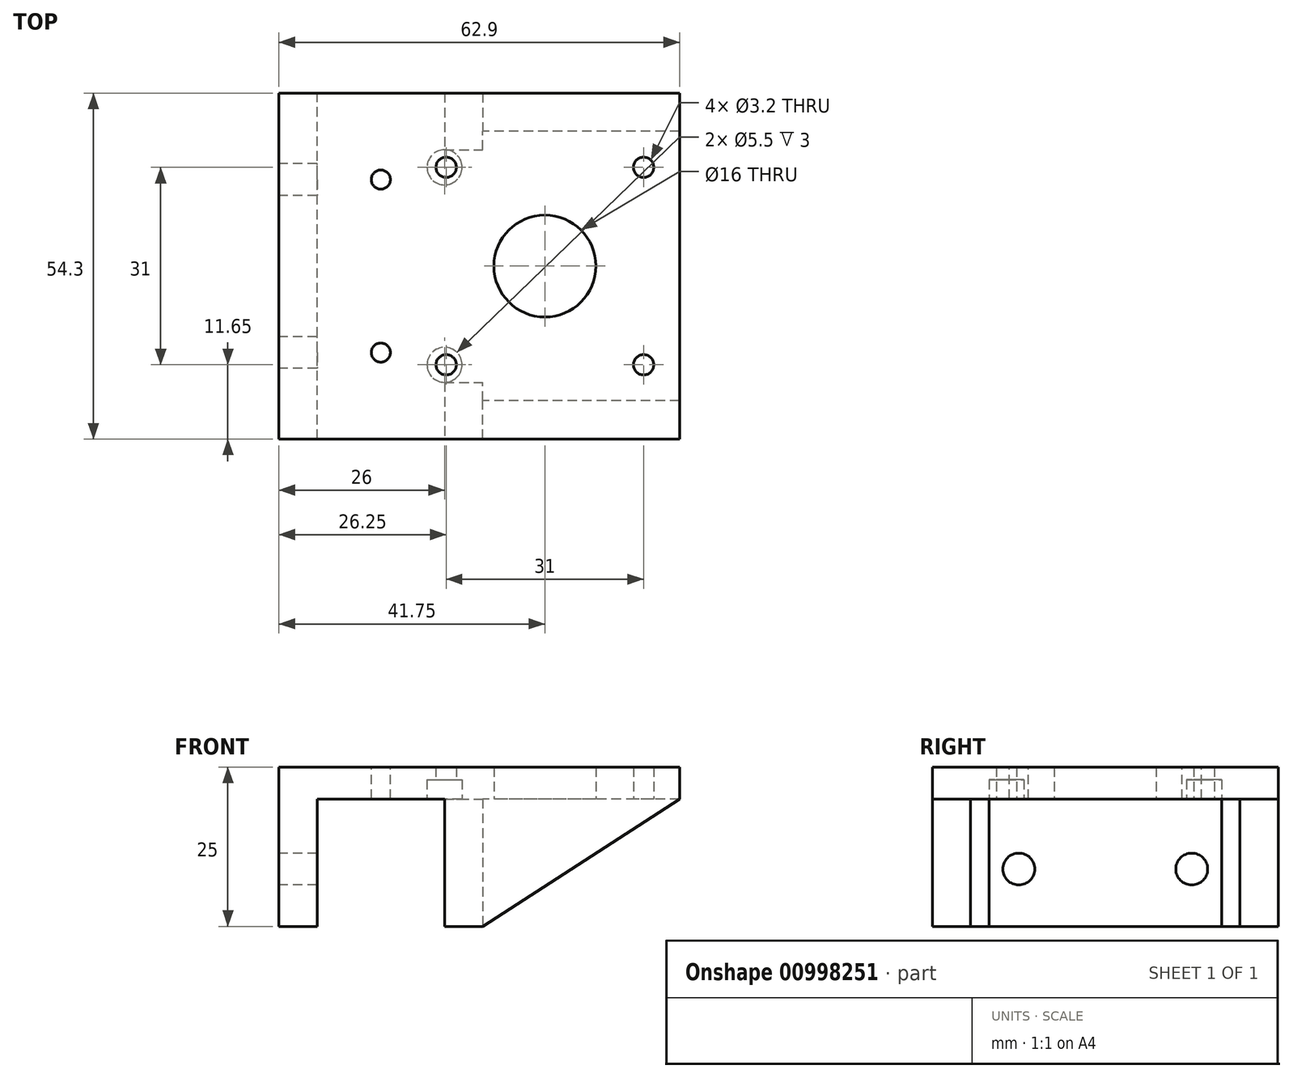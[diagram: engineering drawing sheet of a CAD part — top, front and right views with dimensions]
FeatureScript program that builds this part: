
annotation { "Feature Type Name" : "Feature", "Feature Type Description" : "" }
export const myFeature = defineFeature(function(context is Context, id is Id, definition is map)
    precondition{}
    {
        {
            var Q0;
            Q0=qCreatedBy(makeId("Top.planeOp"),FACE);
            var sketch = newSketch(context, id + "F0", { "sketchPlane" : qUnion([Q0])});
            skPoint(sketch, "E0.middle", {"position": v(0, 0) * mm});
            skCircle(sketch, "E1", {"center": v(0, 0) * mm, "radius": 8 * mm});
            skLineSegment(sketch, "E2.bottom", {"start": v(21.15, -21.15) * mm, "end": v(-21.15, -21.15) * mm});
            skLineSegment(sketch, "E2.top", {"start": v(21.15, 21.15) * mm, "end": v(-21.15, 21.15) * mm});
            skLineSegment(sketch, "E2.left", {"start": v(21.15, -21.15) * mm, "end": v(21.15, 21.15) * mm});
            skLineSegment(sketch, "E3.bottom", {"start": v(-9.75, -21.15) * mm, "end": v(-41.75, -21.15) * mm});
            skLineSegment(sketch, "E3.top", {"start": v(-9.75, 21.15) * mm, "end": v(-41.75, 21.15) * mm});
            skLineSegment(sketch, "E3.left", {"start": v(-9.75, -21.15) * mm, "end": v(-9.75, 21.15) * mm});
            skLineSegment(sketch, "E3.right", {"start": v(-41.75, -21.15) * mm, "end": v(-41.75, 21.15) * mm});
            skCircle(sketch, "E4", {"center": v(-15.5, 15.5) * mm, "radius": 1.6 * mm});
            skCircle(sketch, "E5", {"center": v(15.5, 15.5) * mm, "radius": 1.6 * mm});
            skCircle(sketch, "E6", {"center": v(15.5, -15.5) * mm, "radius": 1.6 * mm});
            skCircle(sketch, "E7", {"center": v(-15.5, -15.5) * mm, "radius": 1.6 * mm});
            skSolve(sketch);
        }
        {
            var Q0;
            Q0=makeQuery(id+"F0.imprint","IMPRINT",FACE,{"disambiguationData":[TD([[makeQuery(id+"F0.imprint","IMPRINT",EDGE,{"derivedFrom":sQuery(id+"F0.wireOp",EDGE,"E1")}),-1.0]])]});
            var Q1;
            {var subQ1=sQuery(id+"F0.wireOp",EDGE,"E3.left");Q1=makeQuery(id+"F0.imprint","IMPRINT",FACE,{"disambiguationData":[TD([[makeQuery(id+"F0.imprint","IMPRINT",EDGE,{"derivedFrom":subQ1}),1.0]])]});}
            extrude(context, id + "F1", {"entities" : qUnion([Q0, Q1]), "depth" : 5 * mm, "offsetDistance" : 25 * mm});
        }
        {
            var Q0;
            Q0=makeQuery(id+"F1.opExtrude","CAP_FACE",FACE,{"disambiguationData":[OSD([sQuery(id+"F0.wireOp",EDGE,"E1"),sQuery(id+"F0.wireOp",EDGE,"E2.bottom"),sQuery(id+"F0.wireOp",EDGE,"E2.top"),sQuery(id+"F0.wireOp",EDGE,"E2.left"),sQuery(id+"F0.wireOp",EDGE,"E3.bottom"),sQuery(id+"F0.wireOp",EDGE,"E3.top"),sQuery(id+"F0.wireOp",EDGE,"E3.right"),sQuery(id+"F0.wireOp",EDGE,"E4"),sQuery(id+"F0.wireOp",EDGE,"E5"),sQuery(id+"F0.wireOp",EDGE,"E6"),sQuery(id+"F0.wireOp",EDGE,"E7")])],"isStart":true});
            var sketch = newSketch(context, id + "F2", { "sketchPlane" : qUnion([Q0])});
            skLineSegment(sketch, "E8", {"start": v(-41.75, 21.15) * mm, "end": v(-35.75, 21.15) * mm});
            skLineSegment(sketch, "E9", {"start": v(-35.75, 21.15) * mm, "end": v(-35.75, -21.15) * mm});
            skLineSegment(sketch, "E10", {"start": v(-35.75, -21.15) * mm, "end": v(-15.75, -21.15) * mm});
            skLineSegment(sketch, "E11", {"start": v(-15.75, -21.15) * mm, "end": v(-15.75, 21.15) * mm});
            skLineSegment(sketch, "E12", {"start": v(-15.75, 21.15) * mm, "end": v(-9.75, 21.15) * mm});
            skLineSegment(sketch, "E13", {"start": v(-9.75, 21.15) * mm, "end": v(-9.75, -21.15) * mm});
            skSolve(sketch);
        }
        {
            var Q0;
            Q0=makeQuery(id+"F2.imprint","IMPRINT",FACE,{"disambiguationData":[TD([[makeQuery(id+"F2.imprint","IMPRINT",EDGE,{"derivedFrom":sQuery(id+"F2.wireOp",EDGE,"E8")}),1.0]])]});
            var Q1;
            {var subQ0=sQuery(id+"F2.wireOp",EDGE,"E12");Q1=makeQuery(id+"F2.imprint","IMPRINT",FACE,{"disambiguationData":[TD([[makeQuery(id+"F2.imprint","IMPRINT",EDGE,{"derivedFrom":subQ0}),1.0]])]});}
            extrude(context, id + "F3", {"entities" : qUnion([Q0, Q1]), "operationType" : NewBodyOperationType.ADD, "depth" : 20 * mm, "offsetDistance" : 25 * mm});
        }
        {
            var Q0;
            {var subQ1=sQuery(id+"F0.wireOp",EDGE,"E3.top");var subQ2=sQuery(id+"F0.wireOp",EDGE,"E2.top");var subQ3=makeQuery(id+"F1.opExtrude","CAP_EDGE",EDGE,{"disambiguationData":[OSD([subQ2,subQ1])],"isStart":true});Q0=makeQuery(id+"F3.boolean.opBoolean","MERGE",FACE,{"derivedFrom":[makeQuery(id+"F1.opExtrude","SWEPT_FACE",FACE,{"disambiguationData":[OSD([subQ2,subQ1])]}),makeQuery(id+"F3.opExtrude","SWEPT_FACE",FACE,{"disambiguationData":[OSD([subQ2,subQ1]),TDD([makeQuery(id+"F2.imprint","IMPRINT",EDGE,{"disambiguationData":[TD([[makeQuery(id+"F2.imprint","INTERSECT",VERTEX,{"derivedFrom":[subQ3,makeQuery(id+"F1.opExtrude","CAP_EDGE",EDGE,{"disambiguationData":[OSD([sQuery(id+"F0.wireOp",EDGE,"E3.right")])],"isStart":true})]}),1.0]])],"derivedFrom":subQ3})])]}),makeQuery(id+"F3.opExtrude","SWEPT_FACE",FACE,{"disambiguationData":[OSD([subQ2,subQ1]),TDD([makeQuery(id+"F2.imprint","IMPRINT",EDGE,{"disambiguationData":[TD([[makeQuery(id+"F2.imprint","INTERSECT",VERTEX,{"derivedFrom":[subQ3,sQuery(id+"F2.wireOp",EDGE,"E13")]}),-1.0]])],"derivedFrom":subQ3})])]})]});}
            var sketch = newSketch(context, id + "F4", { "sketchPlane" : qUnion([Q0])});
            skLineSegment(sketch, "E14", {"start": v(9.75, -20) * mm, "end": v(-21.15, 0) * mm});
            skSolve(sketch);
        }
        {
            var Q0;
            Q0=makeQuery(id+"F4.imprint","IMPRINT",FACE,{"disambiguationData":[TD([[makeQuery(id+"F4.imprint","IMPRINT",EDGE,{"derivedFrom":sQuery(id+"F4.wireOp",EDGE,"E14")}),-1.0]])]});
            var Q1;
            {var subQ3=sQuery(id+"F0.wireOp",EDGE,"E2.top");var subQ5=sQuery(id+"F0.wireOp",EDGE,"E2.left");Q1=makeQuery(id+"F4.imprint","IMPRINT",FACE,{"disambiguationData":[TD([[makeQuery(id+"F4.imprint","IMPRINT",EDGE,{"derivedFrom":makeQuery(id+"F1.opExtrude","SWEPT_EDGE",EDGE,{"disambiguationData":[OSD([subQ3,subQ5])]})}),1.0]])]});}
            extrude(context, id + "F5", {"entities" : qUnion([Q0, Q1]), "operationType" : NewBodyOperationType.ADD, "depth" : 6 * mm, "offsetDistance" : 25 * mm});
        }
        {
            var Q0;
            Q0=makeQuery(id+"F3.boolean.opBoolean","MERGE",FACE,{"derivedFrom":[makeQuery(id+"F1.opExtrude","SWEPT_FACE",FACE,{"disambiguationData":[OSD([sQuery(id+"F0.wireOp",EDGE,"E2.bottom"),sQuery(id+"F0.wireOp",EDGE,"E3.bottom")])]}),makeQuery(id+"F3.opExtrude","SWEPT_FACE",FACE,{"disambiguationData":[OSD([sQuery(id+"F2.wireOp",EDGE,"E8")])]}),makeQuery(id+"F3.opExtrude","SWEPT_FACE",FACE,{"disambiguationData":[OSD([sQuery(id+"F2.wireOp",EDGE,"E12")])]})]});
            var sketch = newSketch(context, id + "F6", { "sketchPlane" : qUnion([Q0])});
            skLineSegment(sketch, "E15", {"start": v(-9.75, -20) * mm, "end": v(21.15, 0) * mm});
            skSolve(sketch);
        }
        {
            var Q0;
            Q0=makeQuery(id+"F6.imprint","IMPRINT",FACE,{"disambiguationData":[TD([[makeQuery(id+"F6.imprint","IMPRINT",EDGE,{"derivedFrom":sQuery(id+"F6.wireOp",EDGE,"E15")}),1.0]])]});
            var Q1;
            {var subQ5=sQuery(id+"F2.wireOp",EDGE,"E8");Q1=makeQuery(id+"F6.imprint","IMPRINT",FACE,{"disambiguationData":[TD([[makeQuery(id+"F6.imprint","IMPRINT",EDGE,{"derivedFrom":makeQuery(id+"F3.opExtrude","CAP_EDGE",EDGE,{"disambiguationData":[OSD([subQ5])],"isStart":false})}),-1.0]])]});}
            extrude(context, id + "F7", {"entities" : qUnion([Q0, Q1]), "operationType" : NewBodyOperationType.ADD, "depth" : 6 * mm, "offsetDistance" : 25 * mm});
        }
        {
            var Q0;
            {var subQ0=sQuery(id+"F0.wireOp",EDGE,"E3.right");Q0=makeQuery(id+"F7.boolean.opBoolean","MERGE",FACE,{"derivedFrom":[makeQuery(id+"F5.boolean.opBoolean","MERGE",FACE,{"derivedFrom":[makeQuery(id+"F3.boolean.opBoolean","MERGE",FACE,{"derivedFrom":[makeQuery(id+"F1.opExtrude","SWEPT_FACE",FACE,{"disambiguationData":[OSD([subQ0])]}),makeQuery(id+"F3.opExtrude","SWEPT_FACE",FACE,{"disambiguationData":[OSD([subQ0])]})]}),makeQuery(id+"F5.opExtrude","SWEPT_FACE",FACE,{"disambiguationData":[OSD([sQuery(id+"F0.wireOp",EDGE,"E2.top"),sQuery(id+"F0.wireOp",EDGE,"E3.top"),subQ0])]})]}),makeQuery(id+"F7.opExtrude","SWEPT_FACE",FACE,{"disambiguationData":[OSD([sQuery(id+"F0.wireOp",EDGE,"E3.bottom"),subQ0,sQuery(id+"F2.wireOp",EDGE,"E8")])]})]});}
            var sketch = newSketch(context, id + "F8", { "sketchPlane" : qUnion([Q0])});
            skLineSegment(sketch, "E16", {"start": v(27.15, 5) * mm, "end": v(27.15, -1) * mm});
            skLineSegment(sketch, "E17", {"start": v(27.15, -1) * mm, "end": v(27.15, -11) * mm});
            skCircle(sketch, "E18", {"center": v(13.58, -11) * mm, "radius": 2.5 * mm});
            skCircle(sketch, "E19", {"center": v(-13.57, -11) * mm, "radius": 2.5 * mm});
            skSolve(sketch);
        }
        {
            var Q0;
            Q0=makeQuery(id+"F8.imprint","IMPRINT",FACE,{"disambiguationData":[TD([[makeQuery(id+"F8.imprint","IMPRINT",EDGE,{"derivedFrom":sQuery(id+"F8.wireOp",EDGE,"E18")}),1.0]])]});
            var Q1;
            Q1=makeQuery(id+"F8.imprint","IMPRINT",FACE,{"disambiguationData":[TD([[makeQuery(id+"F8.imprint","IMPRINT",EDGE,{"derivedFrom":sQuery(id+"F8.wireOp",EDGE,"E19")}),1.0]])]});
            extrude(context, id + "F9", {"entities" : qUnion([Q0, Q1]), "operationType" : NewBodyOperationType.REMOVE, "oppositeDirection" : true, "depth" : 25 * mm, "offsetDistance" : 25 * mm});
        }
        {
            var Q0;
            {var subQ0=sQuery(id+"F2.wireOp",EDGE,"E12");var subQ1=sQuery(id+"F2.wireOp",EDGE,"E11");var subQ2=sQuery(id+"F0.wireOp",EDGE,"E3.top");var subQ3=sQuery(id+"F0.wireOp",EDGE,"E2.top");var subQ4=makeQuery(id+"F1.opExtrude","CAP_EDGE",EDGE,{"disambiguationData":[OSD([subQ3,subQ2])],"isStart":true});var subQ5=sQuery(id+"F2.wireOp",EDGE,"E13");Q0=makeQuery(id+"F7.boolean.opBoolean","MERGE",FACE,{"derivedFrom":[makeQuery(id+"F5.boolean.opBoolean","MERGE",FACE,{"derivedFrom":[makeQuery(id+"F3.opExtrude","CAP_FACE",FACE,{"disambiguationData":[OSD([subQ3,subQ2,sQuery(id+"F0.wireOp",EDGE,"E4"),sQuery(id+"F0.wireOp",EDGE,"E7"),subQ1,subQ0,subQ5])],"isStart":false}),makeQuery(id+"F5.opExtrude","SWEPT_FACE",FACE,{"disambiguationData":[OSD([subQ3,subQ2]),TDD([makeQuery(id+"F4.imprint","IMPRINT",EDGE,{"derivedFrom":makeQuery(id+"F3.opExtrude","CAP_EDGE",EDGE,{"disambiguationData":[OSD([subQ3,subQ2]),TDD([makeQuery(id+"F2.imprint","IMPRINT",EDGE,{"disambiguationData":[TD([[makeQuery(id+"F2.imprint","INTERSECT",VERTEX,{"derivedFrom":[subQ4,subQ5]}),-1.0]])],"derivedFrom":subQ4})])],"isStart":false})})])]})]}),makeQuery(id+"F7.opExtrude","SWEPT_FACE",FACE,{"disambiguationData":[OSD([subQ0])]})]});}
            var sketch = newSketch(context, id + "F10", { "sketchPlane" : qUnion([Q0])});
            skCircle(sketch, "E20", {"center": v(-15.75, -15.5) * mm, "radius": 2.75 * mm});
            skCircle(sketch, "E21", {"center": v(-15.75, 15.5) * mm, "radius": 2.75 * mm});
            skSolve(sketch);
        }
        {
            var Q0;
            {var subQ2=sQuery(id+"F0.wireOp",EDGE,"E4");var subQ13=makeQuery(id+"F3.opExtrude","CAP_EDGE",EDGE,{"disambiguationData":[OSD([subQ2])],"isStart":false});Q0=makeQuery(id+"F10.imprint","IMPRINT",FACE,{"disambiguationData":[TD([[makeQuery(id+"F10.imprint","IMPRINT",EDGE,{"derivedFrom":subQ13}),1.0]])]});}
            var Q1;
            {var subQ2=sQuery(id+"F0.wireOp",EDGE,"E4");var subQ13=makeQuery(id+"F3.opExtrude","CAP_EDGE",EDGE,{"disambiguationData":[OSD([subQ2])],"isStart":false});Q1=makeQuery(id+"F10.imprint","IMPRINT",FACE,{"disambiguationData":[TD([[makeQuery(id+"F10.imprint","IMPRINT",EDGE,{"derivedFrom":subQ13}),-1.0]])]});}
            extrude(context, id + "F11", {"entities" : qUnion([Q0, Q1]), "operationType" : NewBodyOperationType.REMOVE, "oppositeDirection" : true, "depth" : 23 * mm, "offsetDistance" : 25 * mm});
        }
        {
            var Q0;
            {var subQ0=sQuery(id+"F2.wireOp",EDGE,"E12");var subQ1=sQuery(id+"F2.wireOp",EDGE,"E11");var subQ2=sQuery(id+"F0.wireOp",EDGE,"E3.top");var subQ3=sQuery(id+"F0.wireOp",EDGE,"E2.top");var subQ4=makeQuery(id+"F1.opExtrude","CAP_EDGE",EDGE,{"disambiguationData":[OSD([subQ3,subQ2])],"isStart":true});var subQ5=sQuery(id+"F2.wireOp",EDGE,"E13");Q0=makeQuery(id+"F7.boolean.opBoolean","MERGE",FACE,{"derivedFrom":[makeQuery(id+"F5.boolean.opBoolean","MERGE",FACE,{"derivedFrom":[makeQuery(id+"F3.opExtrude","CAP_FACE",FACE,{"disambiguationData":[OSD([subQ3,subQ2,sQuery(id+"F0.wireOp",EDGE,"E4"),sQuery(id+"F0.wireOp",EDGE,"E7"),subQ1,subQ0,subQ5])],"isStart":false}),makeQuery(id+"F5.opExtrude","SWEPT_FACE",FACE,{"disambiguationData":[OSD([subQ3,subQ2]),TDD([makeQuery(id+"F4.imprint","IMPRINT",EDGE,{"derivedFrom":makeQuery(id+"F3.opExtrude","CAP_EDGE",EDGE,{"disambiguationData":[OSD([subQ3,subQ2]),TDD([makeQuery(id+"F2.imprint","IMPRINT",EDGE,{"disambiguationData":[TD([[makeQuery(id+"F2.imprint","INTERSECT",VERTEX,{"derivedFrom":[subQ4,subQ5]}),-1.0]])],"derivedFrom":subQ4})])],"isStart":false})})])]})]}),makeQuery(id+"F7.opExtrude","SWEPT_FACE",FACE,{"disambiguationData":[OSD([subQ0])]})]});}
            var sketch = newSketch(context, id + "F12", { "sketchPlane" : qUnion([Q0])});
            skCircle(sketch, "E22", {"center": v(-15.75, 15.5) * mm, "radius": 2.75 * mm});
            skSolve(sketch);
        }
        {
            var Q0;
            {var subQ5=sQuery(id+"F0.wireOp",EDGE,"E7");var subQ11=makeQuery(id+"F3.opExtrude","CAP_EDGE",EDGE,{"disambiguationData":[OSD([subQ5])],"isStart":false});Q0=makeQuery(id+"F12.imprint","IMPRINT",FACE,{"disambiguationData":[TD([[makeQuery(id+"F12.imprint","IMPRINT",EDGE,{"derivedFrom":subQ11}),1.0]])]});}
            var Q1;
            {var subQ5=sQuery(id+"F0.wireOp",EDGE,"E7");var subQ11=makeQuery(id+"F3.opExtrude","CAP_EDGE",EDGE,{"disambiguationData":[OSD([subQ5])],"isStart":false});Q1=makeQuery(id+"F12.imprint","IMPRINT",FACE,{"disambiguationData":[TD([[makeQuery(id+"F12.imprint","IMPRINT",EDGE,{"derivedFrom":subQ11}),-1.0]])]});}
            extrude(context, id + "F13", {"entities" : qUnion([Q0, Q1]), "operationType" : NewBodyOperationType.REMOVE, "oppositeDirection" : true, "depth" : 23 * mm, "offsetDistance" : 25 * mm});
        }
        {
            var Q0;
            {var subQ0=sQuery(id+"F2.wireOp",EDGE,"E12");var subQ1=sQuery(id+"F2.wireOp",EDGE,"E11");var subQ2=sQuery(id+"F0.wireOp",EDGE,"E3.top");var subQ3=sQuery(id+"F0.wireOp",EDGE,"E2.top");var subQ4=makeQuery(id+"F1.opExtrude","CAP_EDGE",EDGE,{"disambiguationData":[OSD([subQ3,subQ2])],"isStart":true});var subQ5=sQuery(id+"F2.wireOp",EDGE,"E13");Q0=makeQuery(id+"F7.boolean.opBoolean","MERGE",FACE,{"derivedFrom":[makeQuery(id+"F5.boolean.opBoolean","MERGE",FACE,{"derivedFrom":[makeQuery(id+"F3.opExtrude","CAP_FACE",FACE,{"disambiguationData":[OSD([subQ3,subQ2,sQuery(id+"F0.wireOp",EDGE,"E4"),sQuery(id+"F0.wireOp",EDGE,"E7"),subQ1,subQ0,subQ5])],"isStart":false}),makeQuery(id+"F5.opExtrude","SWEPT_FACE",FACE,{"disambiguationData":[OSD([subQ3,subQ2]),TDD([makeQuery(id+"F4.imprint","IMPRINT",EDGE,{"derivedFrom":makeQuery(id+"F3.opExtrude","CAP_EDGE",EDGE,{"disambiguationData":[OSD([subQ3,subQ2]),TDD([makeQuery(id+"F2.imprint","IMPRINT",EDGE,{"disambiguationData":[TD([[makeQuery(id+"F2.imprint","INTERSECT",VERTEX,{"derivedFrom":[subQ4,subQ5]}),-1.0]])],"derivedFrom":subQ4})])],"isStart":false})})])]})]}),makeQuery(id+"F7.opExtrude","SWEPT_FACE",FACE,{"disambiguationData":[OSD([subQ0])]})]});}
            var sketch = newSketch(context, id + "F14", { "sketchPlane" : qUnion([Q0])});
            skLineSegment(sketch, "E23", {"start": v(-15.75, 18.25) * mm, "end": v(-9.75, 18.25) * mm});
            skLineSegment(sketch, "E24", {"start": v(-15.75, -18.25) * mm, "end": v(-9.75, -18.25) * mm});
            skSolve(sketch);
        }
        {
            var Q0;
            {var subQ1=sQuery(id+"F14.wireOp",EDGE,"E23");Q0=makeQuery(id+"F14.imprint","IMPRINT",FACE,{"disambiguationData":[TD([[makeQuery(id+"F14.imprint","IMPRINT",EDGE,{"derivedFrom":subQ1}),-1.0]])]});}
            extrude(context, id + "F15", {"entities" : qUnion([Q0]), "operationType" : NewBodyOperationType.REMOVE, "oppositeDirection" : true, "depth" : 20 * mm, "offsetDistance" : 25 * mm});
        }
        {
            var Q0;
            {var subQ0=sQuery(id+"F0.wireOp",EDGE,"E3.bottom");var subQ1=sQuery(id+"F0.wireOp",EDGE,"E2.bottom");var subQ2=sQuery(id+"F0.wireOp",EDGE,"E3.top");var subQ3=sQuery(id+"F0.wireOp",EDGE,"E2.top");Q0=makeQuery(id+"F7.boolean.opBoolean","MERGE",FACE,{"derivedFrom":[makeQuery(id+"F5.boolean.opBoolean","MERGE",FACE,{"derivedFrom":[makeQuery(id+"F1.opExtrude","CAP_FACE",FACE,{"disambiguationData":[OSD([sQuery(id+"F0.wireOp",EDGE,"E1"),subQ1,subQ3,sQuery(id+"F0.wireOp",EDGE,"E2.left"),subQ0,subQ2,sQuery(id+"F0.wireOp",EDGE,"E3.right"),sQuery(id+"F0.wireOp",EDGE,"E4"),sQuery(id+"F0.wireOp",EDGE,"E5"),sQuery(id+"F0.wireOp",EDGE,"E6"),sQuery(id+"F0.wireOp",EDGE,"E7")])],"isStart":false}),makeQuery(id+"F5.opExtrude","SWEPT_FACE",FACE,{"disambiguationData":[OSD([subQ3,subQ2]),TDD([makeQuery(id+"F4.imprint","IMPRINT",EDGE,{"derivedFrom":makeQuery(id+"F1.opExtrude","CAP_EDGE",EDGE,{"disambiguationData":[OSD([subQ3,subQ2])],"isStart":false})})])]})]}),makeQuery(id+"F7.opExtrude","SWEPT_FACE",FACE,{"disambiguationData":[OSD([subQ1,subQ0]),TDD([makeQuery(id+"F6.imprint","IMPRINT",EDGE,{"derivedFrom":makeQuery(id+"F1.opExtrude","CAP_EDGE",EDGE,{"disambiguationData":[OSD([subQ1,subQ0])],"isStart":false})})])]})]});}
            var sketch = newSketch(context, id + "F16", { "sketchPlane" : qUnion([Q0])});
            skLineSegment(sketch, "E25", {"start": v(-41.75, -27.15) * mm, "end": v(-35.75, -27.15) * mm});
            skLineSegment(sketch, "E26", {"start": v(-35.75, -27.15) * mm, "end": v(-25.75, -27.15) * mm});
            skCircle(sketch, "E27", {"center": v(-25.75, 13.58) * mm, "radius": 1.5 * mm});
            skCircle(sketch, "E28", {"center": v(-25.75, -13.58) * mm, "radius": 1.5 * mm});
            skSolve(sketch);
        }
        {
            var Q0;
            Q0=makeQuery(id+"F16.imprint","IMPRINT",FACE,{"disambiguationData":[TD([[makeQuery(id+"F16.imprint","IMPRINT",EDGE,{"derivedFrom":sQuery(id+"F16.wireOp",EDGE,"E27")}),1.0]])]});
            var Q1;
            Q1=makeQuery(id+"F16.imprint","IMPRINT",FACE,{"disambiguationData":[TD([[makeQuery(id+"F16.imprint","IMPRINT",EDGE,{"derivedFrom":sQuery(id+"F16.wireOp",EDGE,"E28")}),1.0]])]});
            extrude(context, id + "F17", {"entities" : qUnion([Q0, Q1]), "operationType" : NewBodyOperationType.REMOVE, "oppositeDirection" : true, "depth" : 25 * mm, "offsetDistance" : 25 * mm});
        }
    });
